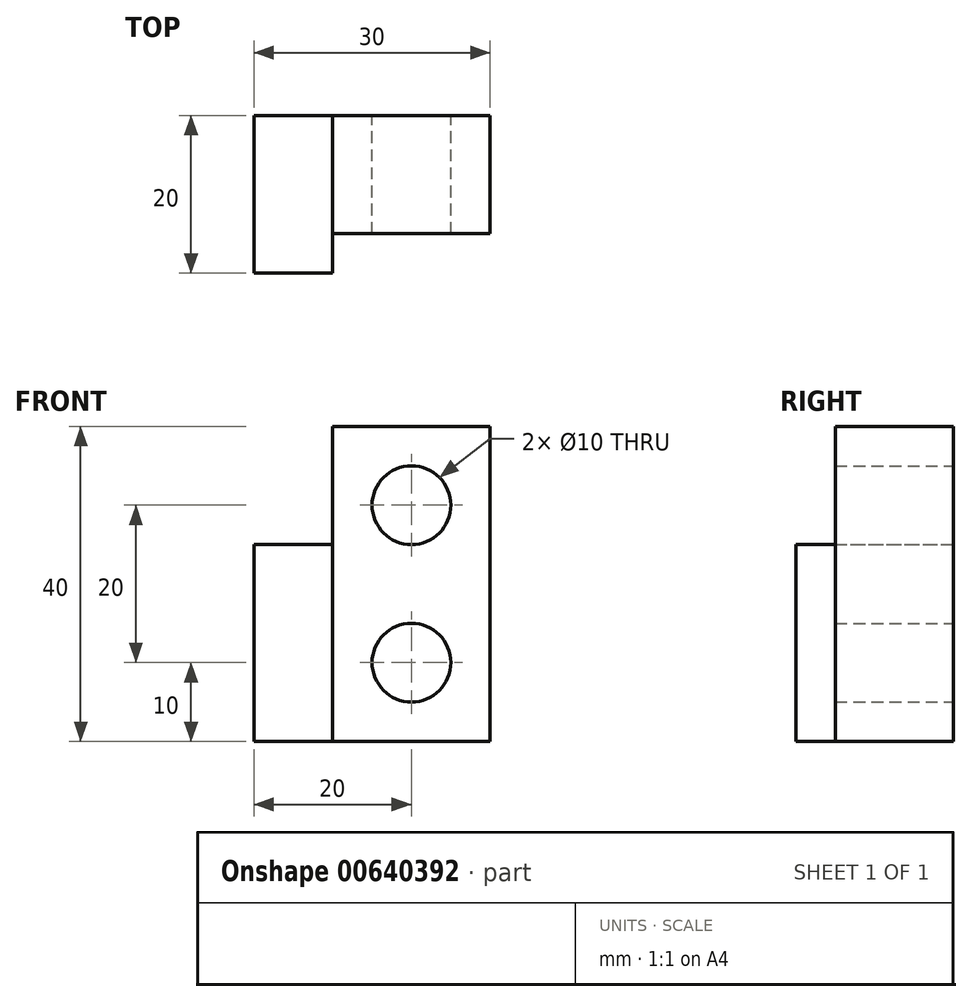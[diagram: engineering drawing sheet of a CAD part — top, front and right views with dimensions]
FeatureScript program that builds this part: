
annotation { "Feature Type Name" : "Feature", "Feature Type Description" : "" }
export const myFeature = defineFeature(function(context is Context, id is Id, definition is map)
    precondition{}
    {
        {
            var Q0;
            Q0=qCreatedBy(makeId("Front.planeOp"),FACE);
            var sketch = newSketch(context, id + "F0", { "sketchPlane" : qUnion([Q0])});
            skLineSegment(sketch, "E0.bottom", {"start": v(-10, 20) * mm, "end": v(10, 20) * mm});
            skLineSegment(sketch, "E0.top", {"start": v(-10, -20) * mm, "end": v(10, -20) * mm});
            skLineSegment(sketch, "E0.left", {"start": v(-10, 20) * mm, "end": v(-10, -20) * mm});
            skLineSegment(sketch, "E0.right", {"start": v(10, 20) * mm, "end": v(10, -20) * mm});
            skPoint(sketch, "E0.middle", {"position": v(0, 0) * mm});
            skLineSegment(sketch, "E1.bottom", {"start": v(-10, -20) * mm, "end": v(-20, -20) * mm});
            skLineSegment(sketch, "E1.top", {"start": v(-10, 5) * mm, "end": v(-20, 5) * mm});
            skLineSegment(sketch, "E1.left", {"start": v(-10, -20) * mm, "end": v(-10, 5) * mm});
            skLineSegment(sketch, "E1.right", {"start": v(-20, -20) * mm, "end": v(-20, 5) * mm});
            skCircle(sketch, "E2", {"center": v(0, -10) * mm, "radius": 5 * mm});
            skCircle(sketch, "E3", {"center": v(0, 10) * mm, "radius": 5 * mm});
            skSolve(sketch);
        }
        {
            var Q0;
            Q0=makeQuery(id+"F0.imprint","IMPRINT",FACE,{"disambiguationData":[TD([[makeQuery(id+"F0.imprint","IMPRINT",EDGE,{"derivedFrom":sQuery(id+"F0.wireOp",EDGE,"E0.bottom")}),-1.0]])]});
            extrude(context, id + "F1", {"entities" : qUnion([Q0]), "depth" : 15 * mm, "offsetDistance" : 25 * mm});
        }
        {
            var Q0;
            Q0=makeQuery(id+"F0.imprint","IMPRINT",FACE,{"disambiguationData":[TD([[makeQuery(id+"F0.imprint","IMPRINT",EDGE,{"derivedFrom":sQuery(id+"F0.wireOp",EDGE,"E1.bottom")}),-1.0]])]});
            extrude(context, id + "F2", {"entities" : qUnion([Q0]), "operationType" : NewBodyOperationType.ADD, "depth" : 20 * mm, "offsetDistance" : 25 * mm});
        }
    });
